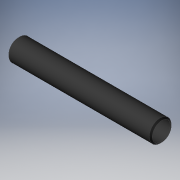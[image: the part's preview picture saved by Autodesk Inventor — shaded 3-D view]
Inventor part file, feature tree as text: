
AUTODESK INVENTOR PART (.ipt)
format: ipt  version: 2019 (Build 230136000, 136)  size: 122,880 bytes
history: native  units: mm
features: other x14, revolve x1, sketch x1
ambient origin geometry x8: Origin, YZ Plane, XZ Plane, XY Plane, X Axis, Y Axis, Z Axis, Center Point
bodies: Solid1 (feature_tree)
feature tree (16):
  revolve  "Revolution1"  [1 undecoded]
  other  "cap_XY"
  other  "cap_YZ"
  other  "cap_ZX"
  other  "cap_X"
  other  "cap_Y"
  other  "cap_Z"
  other  "cap_Center"
  other  "head_XY"
  other  "head_YZ"
  other  "head_ZX"
  other  "head_X"
  other  "head_Y"
  other  "head_Z"
  other  "head_Center"
  sketch  "Sketch_1"  dims[d0=360.0deg]
note: 1 required parameter value undecoded (feature->parameter linkage not recoverable at this tier; creation-order binding heuristic only, values carry confidence <= 0.55)
